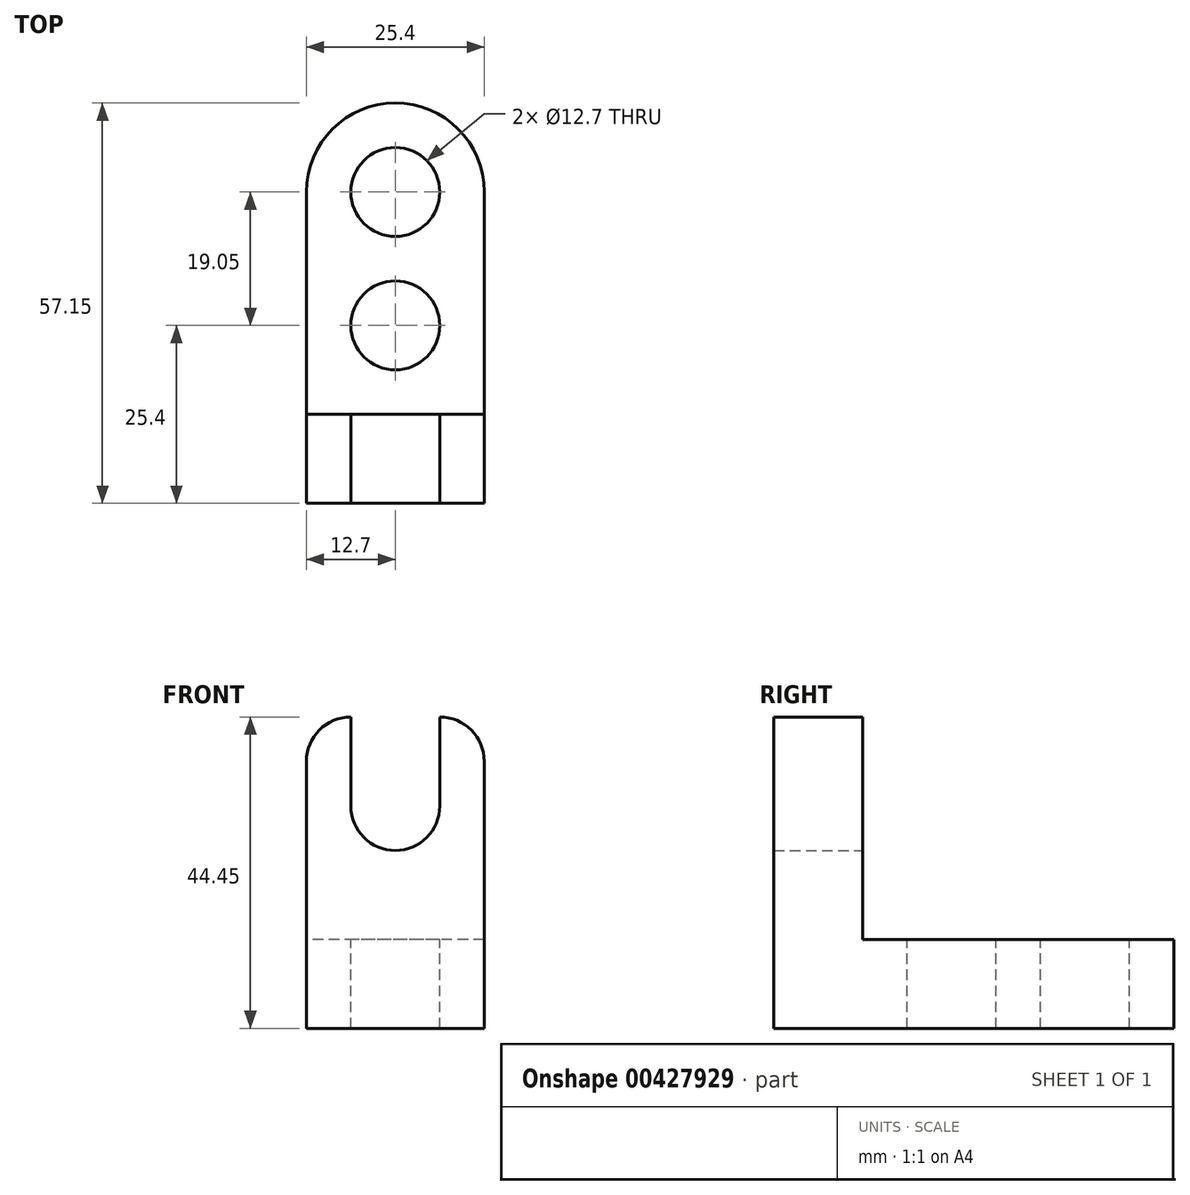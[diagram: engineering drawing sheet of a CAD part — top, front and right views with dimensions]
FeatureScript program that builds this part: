
annotation { "Feature Type Name" : "Feature", "Feature Type Description" : "" }
export const myFeature = defineFeature(function(context is Context, id is Id, definition is map)
    precondition{}
    {
        {
            var Q0;
            Q0=qCreatedBy(makeId("Right.planeOp"),FACE);
            var sketch = newSketch(context, id + "F0", { "sketchPlane" : qUnion([Q0])});
            skLineSegment(sketch, "E0", {"start": v(0, 0) * mm, "end": v(0, 44.45) * mm});
            skLineSegment(sketch, "E1", {"start": v(0, 44.45) * mm, "end": v(12.7, 44.45) * mm});
            skLineSegment(sketch, "E2", {"start": v(12.7, 44.45) * mm, "end": v(12.7, 12.7) * mm});
            skLineSegment(sketch, "E3", {"start": v(12.7, 12.7) * mm, "end": v(57.15, 12.7) * mm});
            skLineSegment(sketch, "E4", {"start": v(57.15, 12.7) * mm, "end": v(57.15, 0) * mm});
            skLineSegment(sketch, "E5", {"start": v(57.15, 0) * mm, "end": v(0, 0) * mm});
            skSolve(sketch);
        }
        {
            var Q0;
            Q0=makeQuery(id+"F0.imprint","IMPRINT",FACE,{"disambiguationData":[TD([[makeQuery(id+"F0.imprint","IMPRINT",EDGE,{"derivedFrom":sQuery(id+"F0.wireOp",EDGE,"E0")}),-1.0]])]});
            extrude(context, id + "F1", {"entities" : qUnion([Q0]), "depth" : 25.4 * mm});
        }
        {
            var Q0;
            Q0=makeQuery(id+"F1.opExtrude","SWEPT_FACE",FACE,{"disambiguationData":[OSD([sQuery(id+"F0.wireOp",EDGE,"E3")])]});
            var sketch = newSketch(context, id + "F2", { "sketchPlane" : qUnion([Q0])});
            skArc(sketch, "E6", {"start": v(25.4, 44.45) * mm, "mid": v(12.7, 57.15) * mm, "end": v(0, 44.45) * mm});
            skCircle(sketch, "E7", {"center": v(12.7, 44.45) * mm, "radius": 6.35 * mm});
            skCircle(sketch, "E8", {"center": v(12.7, 25.4) * mm, "radius": 6.35 * mm});
            skSolve(sketch);
        }
        {
            var Q0;
            {var subQ0=sQuery(id+"F2.wireOp",EDGE,"E6");var subQ1=sQuery(id+"F0.wireOp",EDGE,"E3");var subQ2=makeQuery(id+"F1.opExtrude","CAP_EDGE",EDGE,{"disambiguationData":[OSD([subQ1])],"isStart":true});var subQ3=makeQuery(id+"F2.imprint","INTERSECT",VERTEX,{"derivedFrom":[subQ2,subQ0]});Q0=makeQuery(id+"F2.imprint","IMPRINT",FACE,{"disambiguationData":[TD([[makeQuery(id+"F2.imprint","IMPRINT",EDGE,{"disambiguationData":[TD([[subQ3,1.0]])],"derivedFrom":subQ0}),-1.0]])]});}
            var Q1;
            {var subQ0=sQuery(id+"F2.wireOp",EDGE,"E6");var subQ1=sQuery(id+"F0.wireOp",EDGE,"E3");var subQ2=makeQuery(id+"F1.opExtrude","CAP_EDGE",EDGE,{"disambiguationData":[OSD([subQ1])],"isStart":false});var subQ3=makeQuery(id+"F2.imprint","INTERSECT",VERTEX,{"derivedFrom":[subQ2,subQ0]});Q1=makeQuery(id+"F2.imprint","IMPRINT",FACE,{"disambiguationData":[TD([[makeQuery(id+"F2.imprint","IMPRINT",EDGE,{"disambiguationData":[TD([[subQ3,-1.0]])],"derivedFrom":subQ0}),-1.0]])]});}
            var Q2;
            Q2=makeQuery(id+"F2.imprint","IMPRINT",FACE,{"disambiguationData":[TD([[makeQuery(id+"F2.imprint","IMPRINT",EDGE,{"derivedFrom":sQuery(id+"F2.wireOp",EDGE,"E7")}),1.0]])]});
            var Q3;
            Q3=makeQuery(id+"F2.imprint","IMPRINT",FACE,{"disambiguationData":[TD([[makeQuery(id+"F2.imprint","IMPRINT",EDGE,{"derivedFrom":sQuery(id+"F2.wireOp",EDGE,"E8")}),1.0]])]});
            extrude(context, id + "F3", {"entities" : qUnion([Q0, Q1, Q2, Q3]), "operationType" : NewBodyOperationType.REMOVE, "oppositeDirection" : true, "depth" : 12.7 * mm});
        }
        {
            var Q0;
            Q0=makeQuery(id+"F1.opExtrude","SWEPT_FACE",FACE,{"disambiguationData":[OSD([sQuery(id+"F0.wireOp",EDGE,"E2")])]});
            var sketch = newSketch(context, id + "F4", { "sketchPlane" : qUnion([Q0])});
            skSolve(sketch);
        }
        {
            var Q0;
            {var subQ0=sQuery(id+"F0.wireOp",EDGE,"E2");Q0=makeQuery(id+"F4.imprint","IMPRINT",FACE,{"disambiguationData":[TD([[makeQuery(id+"F4.imprint","IMPRINT",EDGE,{"derivedFrom":makeQuery(id+"F1.opExtrude","CAP_EDGE",EDGE,{"disambiguationData":[OSD([subQ0])],"isStart":true})}),-1.0]])]});}
            var sketch = newSketch(context, id + "F5", { "sketchPlane" : qUnion([Q0])});
            skCircle(sketch, "E9", {"center": v(-12.7, 31.75) * mm, "radius": 6.35 * mm});
            skLineSegment(sketch, "E10", {"start": v(-12.7, 31.75) * mm, "end": v(-19.05, 31.75) * mm});
            skLineSegment(sketch, "E11", {"start": v(-19.05, 31.75) * mm, "end": v(-19.05, 44.45) * mm});
            skLineSegment(sketch, "E12", {"start": v(-12.7, 31.75) * mm, "end": v(-6.35, 31.75) * mm});
            skLineSegment(sketch, "E13", {"start": v(-6.35, 31.75) * mm, "end": v(-6.35, 44.45) * mm});
            skLineSegment(sketch, "E14", {"start": v(-6.35, 44.45) * mm, "end": v(-19.05, 44.45) * mm});
            skSolve(sketch);
        }
        {
            var Q0;
            Q0 = qSketchRegion(id + "F5", true);
            extrude(context, id + "F6", {"entities" : qUnion([Q0]), "operationType" : NewBodyOperationType.REMOVE, "oppositeDirection" : true, "depth" : 12.7 * mm});
        }
        {
            var Q0;
            Q0=makeQuery(id+"F1.opExtrude","SWEPT_FACE",FACE,{"disambiguationData":[OSD([sQuery(id+"F0.wireOp",EDGE,"E0")])]});
            var sketch = newSketch(context, id + "F7", { "sketchPlane" : qUnion([Q0])});
            skArc(sketch, "E15", {"start": v(6.35, 44.45) * mm, "mid": v(1.86, 42.6) * mm, "end": v(0, 38.1) * mm});
            skArc(sketch, "E16", {"start": v(25.4, 38.1) * mm, "mid": v(23.54, 42.6) * mm, "end": v(19.05, 44.45) * mm});
            skSolve(sketch);
        }
        {
            var Q0;
            {var subQ0=sQuery(id+"F7.wireOp",EDGE,"E15");Q0=makeQuery(id+"F7.imprint","IMPRINT",FACE,{"disambiguationData":[TD([[makeQuery(id+"F7.imprint","IMPRINT",EDGE,{"derivedFrom":subQ0}),-1.0]])]});}
            var Q1;
            {var subQ0=sQuery(id+"F7.wireOp",EDGE,"E16");Q1=makeQuery(id+"F7.imprint","IMPRINT",FACE,{"disambiguationData":[TD([[makeQuery(id+"F7.imprint","IMPRINT",EDGE,{"derivedFrom":subQ0}),-1.0]])]});}
            extrude(context, id + "F8", {"entities" : qUnion([Q0, Q1]), "operationType" : NewBodyOperationType.REMOVE, "oppositeDirection" : true, "depth" : 12.7 * mm});
        }
    });
